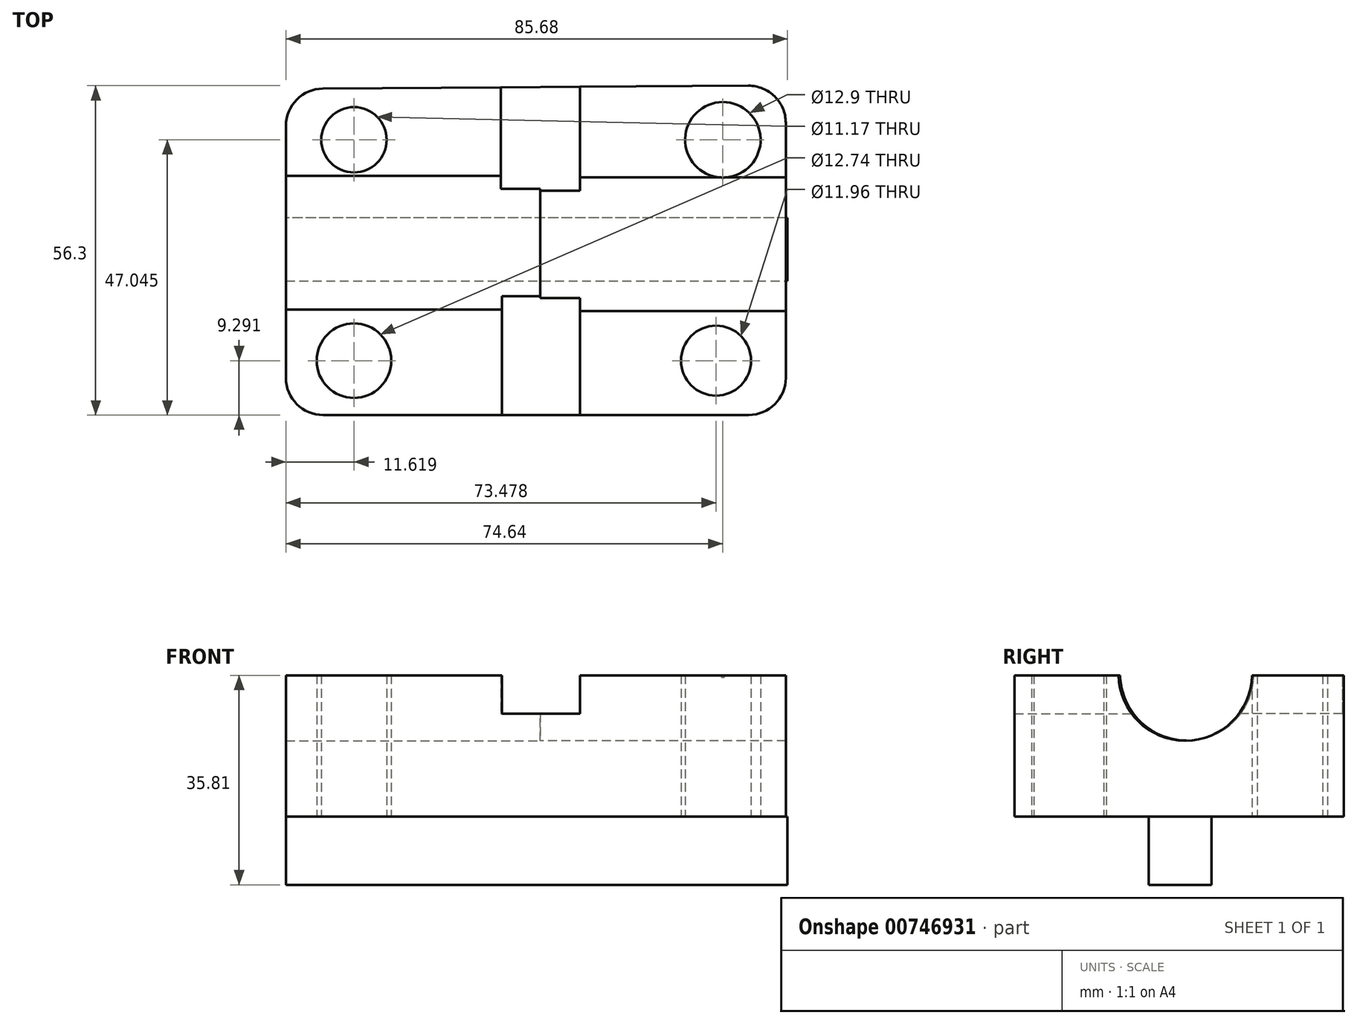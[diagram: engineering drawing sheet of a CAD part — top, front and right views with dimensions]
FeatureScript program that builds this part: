
annotation { "Feature Type Name" : "Feature", "Feature Type Description" : "" }
export const myFeature = defineFeature(function(context is Context, id is Id, definition is map)
    precondition{}
    {
        {
            var Q0;
            Q0=qCreatedBy(makeId("Top.planeOp"),FACE);
            var sketch = newSketch(context, id + "F0", { "sketchPlane" : qUnion([Q0])});
            skLineSegment(sketch, "E0", {"start": v(-43.42, 20.12) * mm, "end": v(-43.42, -22.98) * mm});
            skLineSegment(sketch, "E1", {"start": v(-37.07, -29.33) * mm, "end": v(35.62, -29.33) * mm});
            skLineSegment(sketch, "E2", {"start": v(41.97, -22.98) * mm, "end": v(41.97, 20.62) * mm});
            skLineSegment(sketch, "E3", {"start": v(35.57, 26.97) * mm, "end": v(-37.11, 26.47) * mm});
            skPoint(sketch, "E4.visualSharp", {"position": v(-43.42, 26.43) * mm});
            skArc(sketch, "E4.filletArc", {"start": v(-37.11, 26.47) * mm, "mid": v(-41.57, 24.6) * mm, "end": v(-43.42, 20.12) * mm});
            skPoint(sketch, "E5.visualSharp", {"position": v(-43.42, -29.33) * mm});
            skArc(sketch, "E5.filletArc", {"start": v(-43.42, -22.98) * mm, "mid": v(-41.56, -27.47) * mm, "end": v(-37.07, -29.33) * mm});
            skPoint(sketch, "E6.visualSharp", {"position": v(41.97, -29.33) * mm});
            skArc(sketch, "E6.filletArc", {"start": v(35.62, -29.33) * mm, "mid": v(40.1, -27.47) * mm, "end": v(41.97, -22.98) * mm});
            skPoint(sketch, "E7.visualSharp", {"position": v(41.97, 27) * mm});
            skArc(sketch, "E7.filletArc", {"start": v(41.97, 20.62) * mm, "mid": v(40.1, 25.12) * mm, "end": v(35.57, 26.97) * mm});
            skCircle(sketch, "E8", {"center": v(-31.8, 17.72) * mm, "radius": 5.59 * mm});
            skCircle(sketch, "E9", {"center": v(31.22, 17.72) * mm, "radius": 6.45 * mm});
            skCircle(sketch, "E10", {"center": v(-31.8, -20.04) * mm, "radius": 6.37 * mm});
            skCircle(sketch, "E11", {"center": v(30.06, -20.04) * mm, "radius": 5.98 * mm});
            skSolve(sketch);
        }
        {
            var Q0;
            Q0 = qSketchRegion(id + "F0", true);
            extrude(context, id + "F1", {"entities" : qUnion([Q0]), "depth" : 24.13 * mm, "offsetDistance" : 25.4 * mm});
        }
        {
            var Q0;
            Q0=qCreatedBy(makeId("Front.planeOp"),FACE);
            var sketch = newSketch(context, id + "F2", { "sketchPlane" : qUnion([Q0])});
            skLineSegment(sketch, "E12", {"start": v(-6.74, 26) * mm, "end": v(-6.74, 17.57) * mm});
            skLineSegment(sketch, "E13", {"start": v(-6.74, 17.57) * mm, "end": v(6.82, 17.57) * mm});
            skLineSegment(sketch, "E14", {"start": v(6.82, 17.57) * mm, "end": v(6.82, 26) * mm});
            skLineSegment(sketch, "E15", {"start": v(6.82, 26) * mm, "end": v(-6.74, 26) * mm});
            skSolve(sketch);
        }
        {
            var Q0;
            Q0 = qSketchRegion(id + "F2", true);
            extrude(context, id + "F3", {"entities" : qUnion([Q0]), "operationType" : NewBodyOperationType.REMOVE, "oppositeDirection" : true, "depth" : 37.85 * mm, "offsetDistance" : 25.4 * mm});
        }
        {
            var Q0;
            Q0=qCreatedBy(makeId("Front.planeOp"),FACE);
            var sketch = newSketch(context, id + "F4", { "sketchPlane" : qUnion([Q0])});
            skLineSegment(sketch, "E16", {"start": v(6.82, 17.58) * mm, "end": v(6.82, 29.81) * mm});
            skLineSegment(sketch, "E17", {"start": v(6.82, 29.81) * mm, "end": v(-6.53, 29.81) * mm});
            skLineSegment(sketch, "E18", {"start": v(-6.53, 29.81) * mm, "end": v(-6.53, 17.58) * mm});
            skLineSegment(sketch, "E19", {"start": v(-6.53, 17.58) * mm, "end": v(6.82, 17.58) * mm});
            skSolve(sketch);
        }
        {
            var Q0;
            Q0 = qSketchRegion(id + "F4", true);
            extrude(context, id + "F5", {"entities" : qUnion([Q0]), "operationType" : NewBodyOperationType.REMOVE, "depth" : 46.74 * mm, "offsetDistance" : 25.4 * mm});
        }
        {
            var Q0;
            Q0=qCreatedBy(makeId("Right.planeOp"),FACE);
            var sketch = newSketch(context, id + "F6", { "sketchPlane" : qUnion([Q0])});
            skCircle(sketch, "E20", {"center": v(0.15, 24.4) * mm, "radius": 11.43 * mm});
            skSolve(sketch);
        }
        {
            var Q0;
            Q0=makeQuery(id+"F6.imprint","IMPRINT",FACE,{"disambiguationData":[TD([[makeQuery(id+"F6.imprint","IMPRINT",EDGE,{"derivedFrom":sQuery(id+"F6.wireOp",EDGE,"E20")}),1.0]])]});
            extrude(context, id + "F7", {"entities" : qUnion([Q0]), "operationType" : NewBodyOperationType.REMOVE, "oppositeDirection" : true, "depth" : 53.6 * mm, "offsetDistance" : 25.4 * mm});
        }
        {
            var Q0;
            Q0=qCreatedBy(makeId("Right.planeOp"),FACE);
            var sketch = newSketch(context, id + "F8", { "sketchPlane" : qUnion([Q0])});
            skCircle(sketch, "E21", {"center": v(-0.15, 24.4) * mm, "radius": 11.43 * mm});
            skSolve(sketch);
        }
        {
            var Q0;
            Q0 = qSketchRegion(id + "F8", true);
            extrude(context, id + "F9", {"entities" : qUnion([Q0]), "operationType" : NewBodyOperationType.REMOVE, "depth" : 57.4 * mm, "offsetDistance" : 25.4 * mm});
        }
        {
            var Q0;
            Q0=qCreatedBy(makeId("Top.planeOp"),FACE);
            var sketch = newSketch(context, id + "F10", { "sketchPlane" : qUnion([Q0])});
            skLineSegment(sketch, "E22", {"start": v(-43.42, -6.39) * mm, "end": v(42.26, -6.39) * mm});
            skLineSegment(sketch, "E23", {"start": v(42.26, -6.39) * mm, "end": v(42.26, 4.36) * mm});
            skLineSegment(sketch, "E24", {"start": v(42.26, 4.36) * mm, "end": v(-43.42, 4.36) * mm});
            skLineSegment(sketch, "E25", {"start": v(-43.42, 4.36) * mm, "end": v(-43.42, -6.39) * mm});
            skSolve(sketch);
        }
        {
            var Q0;
            Q0 = qSketchRegion(id + "F10", true);
            extrude(context, id + "F11", {"entities" : qUnion([Q0]), "operationType" : NewBodyOperationType.ADD, "oppositeDirection" : true, "depth" : 11.68 * mm, "offsetDistance" : 25.4 * mm});
        }
    });
